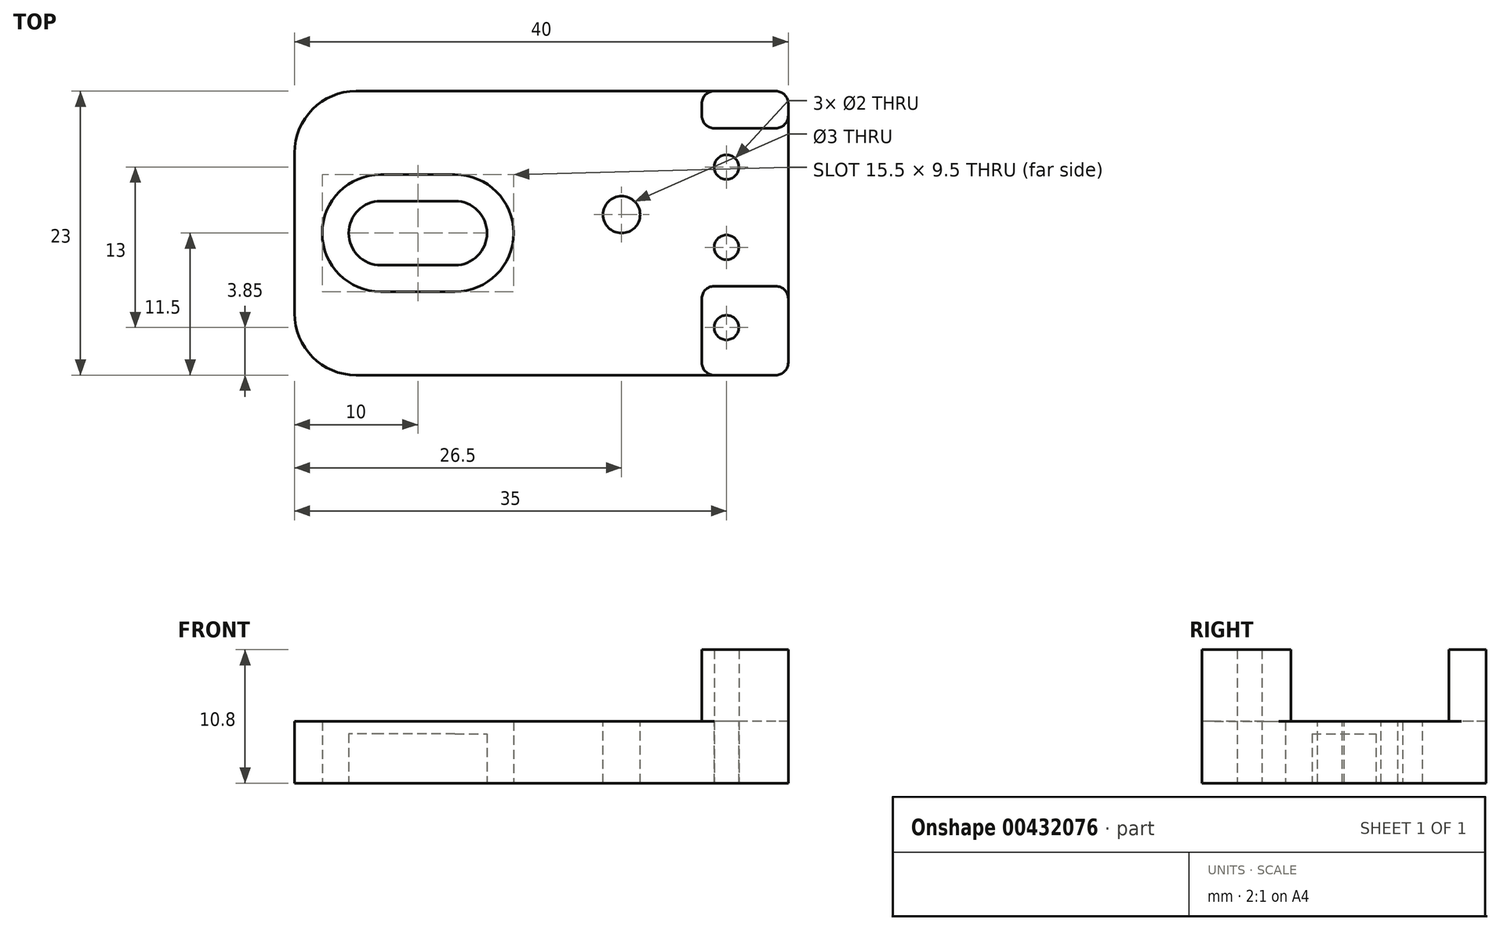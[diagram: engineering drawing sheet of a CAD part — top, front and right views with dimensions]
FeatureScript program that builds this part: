
annotation { "Feature Type Name" : "Feature", "Feature Type Description" : "" }
export const myFeature = defineFeature(function(context is Context, id is Id, definition is map)
    precondition{}
    {
        {
            var Q0;
            Q0=qCreatedBy(makeId("Top.planeOp"),FACE);
            var sketch = newSketch(context, id + "F0", { "sketchPlane" : qUnion([Q0])});
            skLineSegment(sketch, "E0.bottom", {"start": v(10, -11.5) * mm, "end": v(-10, -11.5) * mm});
            skLineSegment(sketch, "E0.top", {"start": v(10, 11.5) * mm, "end": v(-10, 11.5) * mm});
            skLineSegment(sketch, "E0.left", {"start": v(10, -11.5) * mm, "end": v(10, 11.5) * mm});
            skLineSegment(sketch, "E0.right", {"start": v(-10, -11.5) * mm, "end": v(-10, 11.5) * mm});
            skPoint(sketch, "E0.middle", {"position": v(0, 0) * mm});
            skLineSegment(sketch, "E1.bottom", {"start": v(10, -11.5) * mm, "end": v(30, -11.5) * mm});
            skLineSegment(sketch, "E1.top", {"start": v(10, 11.5) * mm, "end": v(30, 11.5) * mm});
            skLineSegment(sketch, "E1.right", {"start": v(30, -11.5) * mm, "end": v(30, 11.5) * mm});
            skLineSegment(sketch, "E2", {"start": v(3, 0) * mm, "end": v(-3, 0) * mm});
            skArc(sketch, "E3.0.startCap", {"start": v(3, 2.6) * mm, "mid": v(5.6, 0) * mm, "end": v(3, -2.6) * mm});
            skArc(sketch, "E3.0.endCap", {"start": v(-3, -2.6) * mm, "mid": v(-5.6, 0) * mm, "end": v(-3, 2.6) * mm});
            skLineSegment(sketch, "E3.0.left", {"start": v(3, -2.6) * mm, "end": v(-3, -2.6) * mm});
            skLineSegment(sketch, "E3.0.right", {"start": v(3, 2.6) * mm, "end": v(-3, 2.6) * mm});
            skArc(sketch, "E4.0.startCap", {"start": v(3, 4.75) * mm, "mid": v(7.75, 0) * mm, "end": v(3, -4.75) * mm});
            skArc(sketch, "E4.0.endCap", {"start": v(-3, -4.75) * mm, "mid": v(-7.75, 0) * mm, "end": v(-3, 4.75) * mm});
            skLineSegment(sketch, "E4.0.left", {"start": v(3, -4.75) * mm, "end": v(-3, -4.75) * mm});
            skLineSegment(sketch, "E4.0.right", {"start": v(3, 4.75) * mm, "end": v(-3, 4.75) * mm});
            skSolve(sketch);
        }
        {
            var Q0;
            Q0=makeQuery(id+"F0.imprint","IMPRINT",FACE,{"disambiguationData":[TD([[makeQuery(id+"F0.imprint","IMPRINT",EDGE,{"derivedFrom":sQuery(id+"F0.wireOp",EDGE,"E0.bottom")}),-1.0]])]});
            var Q1;
            Q1=makeQuery(id+"F0.imprint","IMPRINT",FACE,{"disambiguationData":[TD([[makeQuery(id+"F0.imprint","IMPRINT",EDGE,{"derivedFrom":sQuery(id+"F0.wireOp",EDGE,"E1.bottom")}),1.0]])]});
            extrude(context, id + "F1", {"entities" : qUnion([Q0, Q1]), "depth" : 5 * mm});
        }
        {
            var Q0;
            Q0=makeQuery(id+"F1.opExtrude","CAP_FACE",FACE,{"disambiguationData":[OSD([sQuery(id+"F0.wireOp",EDGE,"E0.bottom"),sQuery(id+"F0.wireOp",EDGE,"E0.top"),sQuery(id+"F0.wireOp",EDGE,"E0.right"),sQuery(id+"F0.wireOp",EDGE,"E1.bottom"),sQuery(id+"F0.wireOp",EDGE,"E1.top"),sQuery(id+"F0.wireOp",EDGE,"E1.right"),sQuery(id+"F0.wireOp",EDGE,"E4.0.startCap"),sQuery(id+"F0.wireOp",EDGE,"E4.0.endCap"),sQuery(id+"F0.wireOp",EDGE,"E4.0.left"),sQuery(id+"F0.wireOp",EDGE,"E4.0.right")])],"isStart":false});
            var sketch = newSketch(context, id + "F2", { "sketchPlane" : qUnion([Q0])});
            skLineSegment(sketch, "E5.bottom", {"start": v(30, 11.5) * mm, "end": v(23, 11.5) * mm});
            skLineSegment(sketch, "E5.top", {"start": v(30, 8.5) * mm, "end": v(23, 8.5) * mm});
            skLineSegment(sketch, "E5.left", {"start": v(30, 11.5) * mm, "end": v(30, 8.5) * mm});
            skLineSegment(sketch, "E5.right", {"start": v(23, 11.5) * mm, "end": v(23, 8.5) * mm});
            skLineSegment(sketch, "E6.bottom", {"start": v(30, -11.5) * mm, "end": v(23, -11.5) * mm});
            skLineSegment(sketch, "E6.top", {"start": v(30, -4.3) * mm, "end": v(23, -4.3) * mm});
            skLineSegment(sketch, "E6.left", {"start": v(30, -11.5) * mm, "end": v(30, -4.3) * mm});
            skLineSegment(sketch, "E6.right", {"start": v(23, -11.5) * mm, "end": v(23, -4.3) * mm});
            skCircle(sketch, "E7", {"center": v(25, 5.35) * mm, "radius": 1 * mm});
            skCircle(sketch, "E8", {"center": v(25, -1.15) * mm, "radius": 1 * mm});
            skCircle(sketch, "E9", {"center": v(25, -7.65) * mm, "radius": 1 * mm});
            skCircle(sketch, "E10", {"center": v(16.5, 1.5) * mm, "radius": 1.5 * mm});
            skPoint(sketch, "E10.centerSnap0", {"position": v(30, 0) * mm});
            skSolve(sketch);
        }
        {
            var Q0;
            Q0=makeQuery(id+"F2.imprint","IMPRINT",FACE,{"disambiguationData":[TD([[makeQuery(id+"F2.imprint","IMPRINT",EDGE,{"derivedFrom":sQuery(id+"F2.wireOp",EDGE,"E5.bottom")}),1.0]])]});
            var Q1;
            Q1=makeQuery(id+"F2.imprint","IMPRINT",FACE,{"disambiguationData":[TD([[makeQuery(id+"F2.imprint","IMPRINT",EDGE,{"derivedFrom":sQuery(id+"F2.wireOp",EDGE,"E6.bottom")}),-1.0]])]});
            extrude(context, id + "F3", {"entities" : qUnion([Q0, Q1]), "operationType" : NewBodyOperationType.ADD, "depth" : 5.8 * mm});
        }
        {
            var Q0;
            Q0=makeQuery(id+"F2.imprint","IMPRINT",FACE,{"disambiguationData":[TD([[makeQuery(id+"F2.imprint","IMPRINT",EDGE,{"derivedFrom":sQuery(id+"F2.wireOp",EDGE,"E7")}),1.0]])]});
            var Q1;
            Q1=makeQuery(id+"F2.imprint","IMPRINT",FACE,{"disambiguationData":[TD([[makeQuery(id+"F2.imprint","IMPRINT",EDGE,{"derivedFrom":sQuery(id+"F2.wireOp",EDGE,"E8")}),1.0]])]});
            var Q2;
            Q2=makeQuery(id+"F2.imprint","IMPRINT",FACE,{"disambiguationData":[TD([[makeQuery(id+"F2.imprint","IMPRINT",EDGE,{"derivedFrom":sQuery(id+"F2.wireOp",EDGE,"E9")}),1.0]])]});
            extrude(context, id + "F4", {"entities" : qUnion([Q0, Q1, Q2]), "operationType" : NewBodyOperationType.REMOVE, "endBound" : BoundingType.THROUGH_ALL, "oppositeDirection" : true, "depth" : 25 * mm});
        }
        {
            var Q0;
            {var subQ0=sQuery(id+"F0.wireOp",EDGE,"E0.top");Q0=makeQuery(id+"FR0FlmJJfxahWxj_1.opChamfer","BLEND_EDGE",EDGE,{"blendedFrom":[makeQuery(id+"F1.opExtrude","SWEPT_EDGE",EDGE,{"disambiguationData":[OSD([subQ0,sQuery(id+"F0.wireOp",EDGE,"E0.right")])]}),makeQuery(id+"F3.boolean.opBoolean","MERGE",FACE,{"derivedFrom":[makeQuery(id+"F1.opExtrude","SWEPT_FACE",FACE,{"disambiguationData":[OSD([subQ0,sQuery(id+"F0.wireOp",EDGE,"E1.top")])]}),makeQuery(id+"F3.opExtrude","SWEPT_FACE",FACE,{"disambiguationData":[OSD([sQuery(id+"F2.wireOp",EDGE,"E5.bottom")])]})]})],"blendedInto":[makeQuery(id+"F3.boolean.opBoolean","MERGE",FACE,{"derivedFrom":[makeQuery(id+"F1.opExtrude","SWEPT_FACE",FACE,{"disambiguationData":[OSD([subQ0,sQuery(id+"F0.wireOp",EDGE,"E1.top")])]}),makeQuery(id+"F3.opExtrude","SWEPT_FACE",FACE,{"disambiguationData":[OSD([sQuery(id+"F2.wireOp",EDGE,"E5.bottom")])]})]})]});}
            var Q1;
            {var subQ0=sQuery(id+"F0.wireOp",EDGE,"E0.right");Q1=makeQuery(id+"FR0FlmJJfxahWxj_1.opChamfer","BLEND_EDGE",EDGE,{"blendedFrom":[makeQuery(id+"F1.opExtrude","SWEPT_EDGE",EDGE,{"disambiguationData":[OSD([sQuery(id+"F0.wireOp",EDGE,"E0.top"),subQ0])]}),makeQuery(id+"F1.opExtrude","SWEPT_FACE",FACE,{"disambiguationData":[OSD([subQ0])]})],"blendedInto":[makeQuery(id+"F1.opExtrude","SWEPT_FACE",FACE,{"disambiguationData":[OSD([subQ0])]})]});}
            var Q2;
            Q2=makeQuery(id+"F1.opExtrude","SWEPT_EDGE",EDGE,{"disambiguationData":[OSD([sQuery(id+"F0.wireOp",EDGE,"E0.bottom"),sQuery(id+"F0.wireOp",EDGE,"E0.right")])]});
            var Q3;
            Q3=makeQuery(id+"F1.opExtrude","SWEPT_EDGE",EDGE,{"disambiguationData":[OSD([sQuery(id+"F0.wireOp",EDGE,"E0.top"),sQuery(id+"F0.wireOp",EDGE,"E0.right")])]});
            fillet(context, id + "F5", {"entities" : qUnion([Q0, Q1, Q2, Q3]), "radius" : 5 * mm, "tangentPropagation" : true, "allowEdgeOverflow" : false});
        }
        {
            var Q0;
            Q0=makeQuery(id+"F3.boolean.opBoolean","MERGE",EDGE,{"derivedFrom":[makeQuery(id+"F1.opExtrude","SWEPT_EDGE",EDGE,{"disambiguationData":[OSD([sQuery(id+"F0.wireOp",EDGE,"E1.bottom"),sQuery(id+"F0.wireOp",EDGE,"E1.right")])]}),makeQuery(id+"F3.opExtrude","SWEPT_EDGE",EDGE,{"disambiguationData":[OSD([sQuery(id+"F2.wireOp",EDGE,"E6.bottom"),sQuery(id+"F2.wireOp",EDGE,"E6.left")])]})]});
            var Q1;
            Q1=makeQuery(id+"F3.boolean.opBoolean","MERGE",EDGE,{"derivedFrom":[makeQuery(id+"F1.opExtrude","SWEPT_EDGE",EDGE,{"disambiguationData":[OSD([sQuery(id+"F0.wireOp",EDGE,"E1.top"),sQuery(id+"F0.wireOp",EDGE,"E1.right")])]}),makeQuery(id+"F3.opExtrude","SWEPT_EDGE",EDGE,{"disambiguationData":[OSD([sQuery(id+"F2.wireOp",EDGE,"E5.bottom"),sQuery(id+"F2.wireOp",EDGE,"E5.left")])]})]});
            fillet(context, id + "F6", {"entities" : qUnion([Q0, Q1]), "radius" : 1 * mm, "tangentPropagation" : true, "allowEdgeOverflow" : false});
        }
        {
            var Q0;
            Q0=makeQuery(id+"F3.opExtrude","SWEPT_EDGE",EDGE,{"disambiguationData":[OSD([sQuery(id+"F2.wireOp",EDGE,"E5.top"),sQuery(id+"F2.wireOp",EDGE,"E5.right")])]});
            var Q1;
            Q1=makeQuery(id+"F3.opExtrude","SWEPT_EDGE",EDGE,{"disambiguationData":[OSD([sQuery(id+"F2.wireOp",EDGE,"E6.top"),sQuery(id+"F2.wireOp",EDGE,"E6.right")])]});
            var Q2;
            Q2=makeQuery(id+"F3.opExtrude","SWEPT_EDGE",EDGE,{"disambiguationData":[OSD([sQuery(id+"F0.wireOp",EDGE,"E1.right"),sQuery(id+"F2.wireOp",EDGE,"E6.top"),sQuery(id+"F2.wireOp",EDGE,"E6.left")])]});
            var Q3;
            Q3=makeQuery(id+"F3.opExtrude","SWEPT_EDGE",EDGE,{"disambiguationData":[OSD([sQuery(id+"F0.wireOp",EDGE,"E1.right"),sQuery(id+"F2.wireOp",EDGE,"E5.top"),sQuery(id+"F2.wireOp",EDGE,"E5.left")])]});
            var Q4;
            Q4=makeQuery(id+"F3.opExtrude","SWEPT_EDGE",EDGE,{"disambiguationData":[OSD([sQuery(id+"F0.wireOp",EDGE,"E0.bottom"),sQuery(id+"F0.wireOp",EDGE,"E1.bottom"),sQuery(id+"F2.wireOp",EDGE,"E6.bottom"),sQuery(id+"F2.wireOp",EDGE,"E6.right")])]});
            var Q5;
            Q5=makeQuery(id+"F3.opExtrude","SWEPT_EDGE",EDGE,{"disambiguationData":[OSD([sQuery(id+"F0.wireOp",EDGE,"E0.top"),sQuery(id+"F0.wireOp",EDGE,"E1.top"),sQuery(id+"F2.wireOp",EDGE,"E5.bottom"),sQuery(id+"F2.wireOp",EDGE,"E5.right")])]});
            fillet(context, id + "F7", {"entities" : qUnion([Q0, Q1, Q2, Q3, Q4, Q5]), "radius" : 1 * mm, "tangentPropagation" : true, "allowEdgeOverflow" : false});
        }
        {
            var Q0;
            Q0=makeQuery(id+"F0.imprint","IMPRINT",FACE,{"disambiguationData":[TD([[makeQuery(id+"F0.imprint","IMPRINT",EDGE,{"derivedFrom":sQuery(id+"F0.wireOp",EDGE,"E3.0.startCap")}),1.0]])]});
            extrude(context, id + "F8", {"entities" : qUnion([Q0]), "operationType" : NewBodyOperationType.ADD, "depth" : 4 * mm});
        }
        {
            var Q0;
            Q0=makeQuery(id+"F2.imprint","IMPRINT",FACE,{"disambiguationData":[TD([[makeQuery(id+"F2.imprint","IMPRINT",EDGE,{"derivedFrom":sQuery(id+"F2.wireOp",EDGE,"E10")}),1.0]])]});
            extrude(context, id + "F9", {"entities" : qUnion([Q0]), "operationType" : NewBodyOperationType.REMOVE, "endBound" : BoundingType.THROUGH_ALL, "oppositeDirection" : true, "depth" : 25 * mm});
        }
    });
